# Revit family: NLRS_57_AIR_UN_airflow-arrow-open-end-round-duct-out_sacs
name_source: partatom
category: Air Terminals
units: mm (PartAtom-declared; Revit-internal decimal feet)

## family parameters
Always vertical = Yes
Cut with Voids When Loaded = No
Part Type = Normal
Room Calculation Point = No
Round Connector Dimension = Use Diameter
Shared = No
Work Plane-Based = No

## types (3) — shared parameters
Description = Round open end, airflow duct OUT
IfcDescription = Round open end, airflow duct OUT
IfcExportAs = IfcAirTerminal
IfcExportType = OPEN END
Manufacturer = Solid Air Climate Systems
Model = Airflow arrow - duct OUT
NLRS_C_content_datum_uitgifte = 28-05-2024
NLRS_C_content_provider = Solid Air Climate Systems
NLRS_C_content_versie = 1.21.01
NLRS_C_description = Round open end, airflow duct OUT
NLRS_C_model = Airflow arrow - duct OUT
zero-valued in all types: Default Elevation

## per-type parameters (varying)
| type | Assembly Code | Size_multiplier | URL |
| Size 1 | 57.00 | 1 | https://solid-air.nl |
| Size 1.5 |  | 1.5 |  |
| Size 2 |  | 2 |  |

## geometry (parser evidence)
native form markers: Sweep x8
no freeform markers — native parametric forms only
